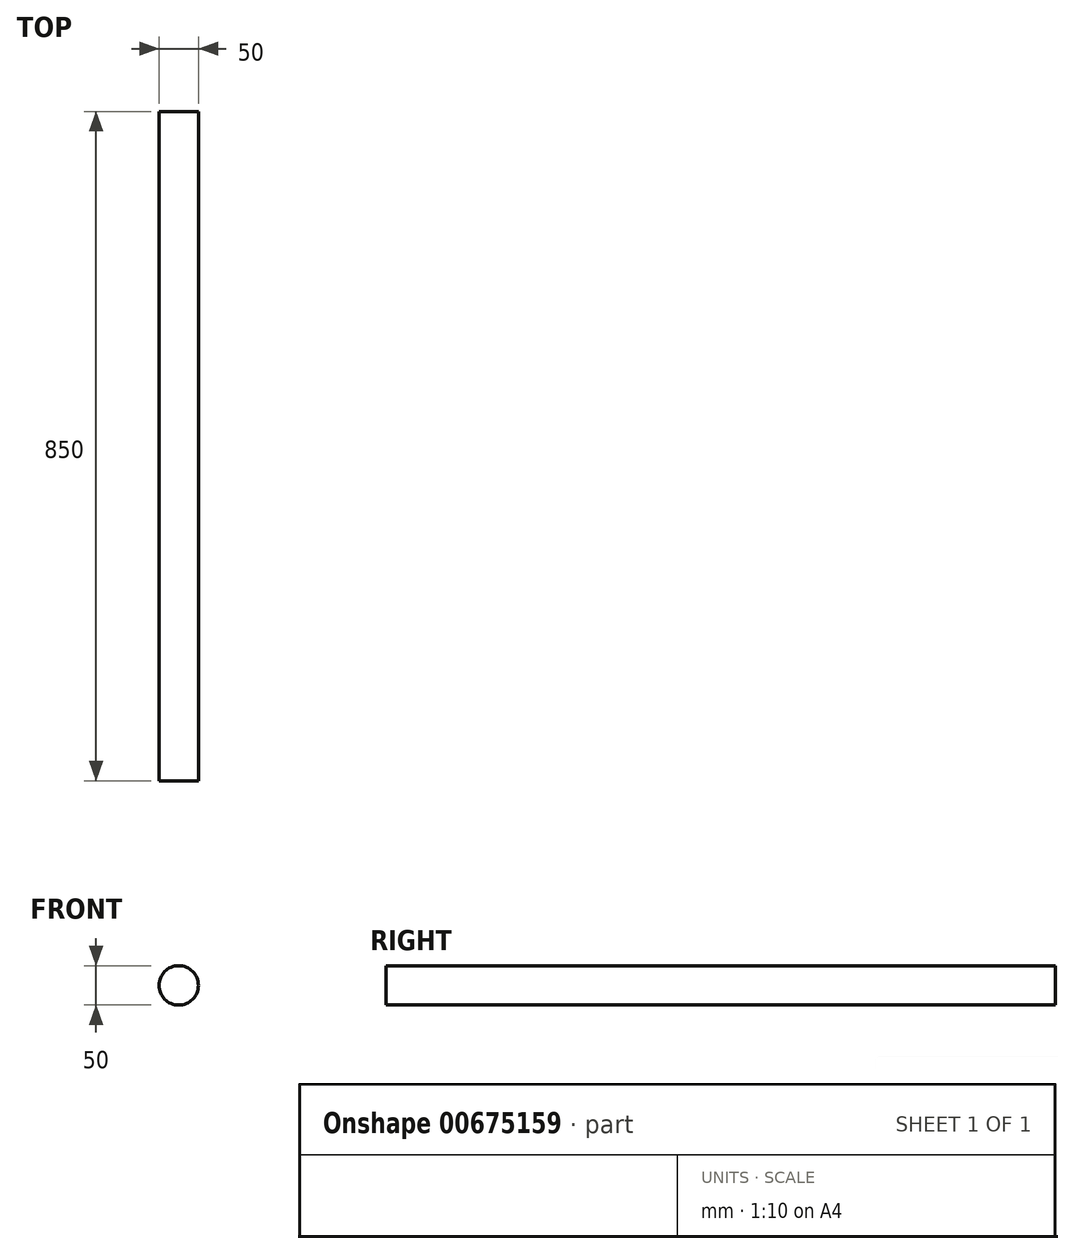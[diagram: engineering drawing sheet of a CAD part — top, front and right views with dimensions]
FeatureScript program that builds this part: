
annotation { "Feature Type Name" : "Feature", "Feature Type Description" : "" }
export const myFeature = defineFeature(function(context is Context, id is Id, definition is map)
    precondition{}
    {
        {
            var Q0;
            Q0=qCreatedBy(makeId("Front.planeOp"),FACE);
            var sketch = newSketch(context, id + "F0", { "sketchPlane" : qUnion([Q0])});
            skCircle(sketch, "E0", {"center": v(0, 0) * mm, "radius": 25 * mm});
            skSolve(sketch);
        }
        {
            var Q0;
            Q0=makeQuery(id+"F0.imprint","IMPRINT",FACE,{"disambiguationData":[TD([[makeQuery(id+"F0.imprint","IMPRINT",EDGE,{"derivedFrom":sQuery(id+"F0.wireOp",EDGE,"E0")}),1.0]])]});
            extrude(context, id + "F1", {"entities" : qUnion([Q0]), "depth" : 750 * mm, "offsetDistance" : 25 * mm});
        }
        {
            var Q0;
            Q0=qSketchRegion(id+"F0",true);
            extrude(context, id + "F2", {"entities" : qUnion([Q0]), "operationType" : NewBodyOperationType.ADD, "oppositeDirection" : true, "depth" : 100 * mm, "offsetDistance" : 25 * mm});
        }
    });
